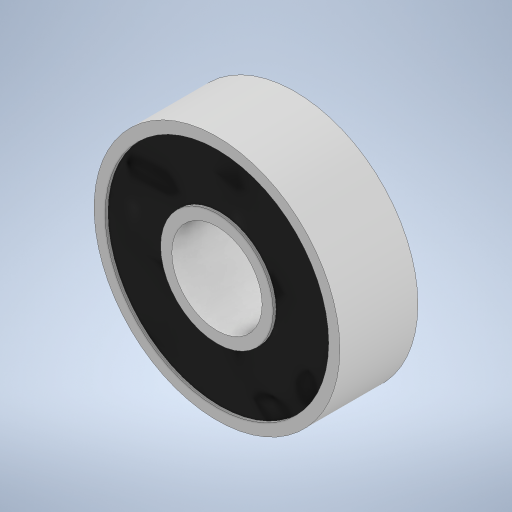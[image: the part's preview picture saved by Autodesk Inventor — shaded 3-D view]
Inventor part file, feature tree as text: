
AUTODESK INVENTOR PART (.ipt)
format: ipt  version: 2023 (Build 270158000, 158)  size: 257,024 bytes
history: native  units: mm
features: extrude x3, sketch x3
ambient origin geometry x8: Origin, YZ Plane, XZ Plane, XY Plane, X Axis, Y Axis, Z Axis, Center Point
bodies: Solid1 (feature_tree)
feature tree (6):
  extrude  "Extrusion1"  Depth=8.1mm
  extrude  "Extrusion2"  Depth=7.0mm
  extrude  "Extrusion3"  Depth=0.25mm TaperAngle=0.0deg
  sketch  "Sketch1"  dims[d0=22.05mm d1=8.1mm]
  sketch  "Sketch2"  dims[d2=7.0mm d3=0.0mm d4=1.0mm]
  sketch  "Sketch3"  dims[d5=1.0mm d6=0.25mm d7=0.0mm d8=0.25mm d9=0.0mm]
